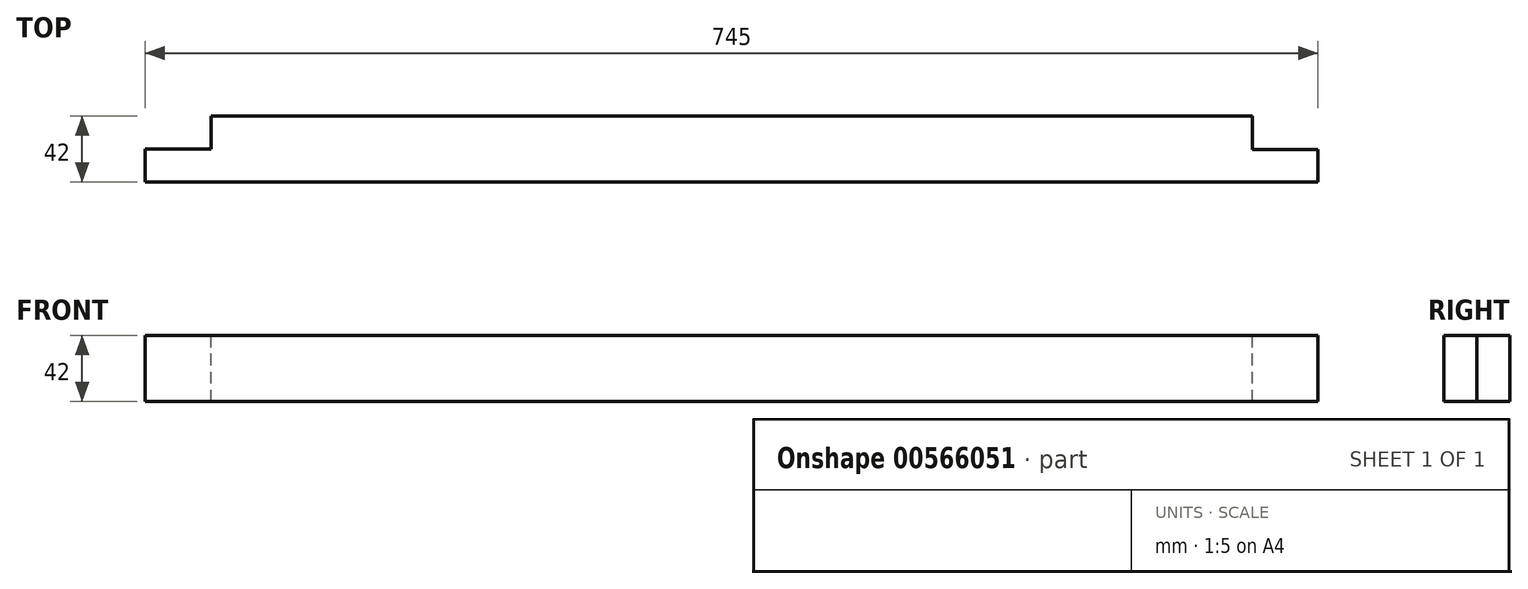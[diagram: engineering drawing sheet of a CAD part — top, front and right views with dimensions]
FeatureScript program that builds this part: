
annotation { "Feature Type Name" : "Feature", "Feature Type Description" : "" }
export const myFeature = defineFeature(function(context is Context, id is Id, definition is map)
    precondition{}
    {
        {
            var Q0;
            Q0=qCreatedBy(makeId("Top.planeOp"),FACE);
            var sketch = newSketch(context, id + "F0", { "sketchPlane" : qUnion([Q0])});
            skLineSegment(sketch, "E0.bottom", {"start": v(-348.32, -28.54) * mm, "end": v(396.68, -28.54) * mm});
            skLineSegment(sketch, "E0.top", {"start": v(-348.32, -70.54) * mm, "end": v(396.68, -70.54) * mm});
            skLineSegment(sketch, "E0.left", {"start": v(-348.32, -28.54) * mm, "end": v(-348.32, -70.54) * mm});
            skLineSegment(sketch, "E0.right", {"start": v(396.68, -28.54) * mm, "end": v(396.68, -70.54) * mm});
            skSolve(sketch);
        }
        {
            var Q0;
            Q0 = qSketchRegion(id + "F0", true);
            extrude(context, id + "F1", {"entities" : qUnion([Q0]), "depth" : 42 * mm, "offsetDistance" : 25 * mm});
        }
        {
            var Q0;
            Q0=makeQuery(id+"F1.opExtrude","CAP_FACE",FACE,{"disambiguationData":[OSD([sQuery(id+"F0.wireOp",EDGE,"E0.bottom"),sQuery(id+"F0.wireOp",EDGE,"E0.top"),sQuery(id+"F0.wireOp",EDGE,"E0.left"),sQuery(id+"F0.wireOp",EDGE,"E0.right")])],"isStart":false});
            var sketch = newSketch(context, id + "F2", { "sketchPlane" : qUnion([Q0])});
            skLineSegment(sketch, "E1.bottom", {"start": v(396.68, -28.54) * mm, "end": v(354.96, -28.54) * mm});
            skLineSegment(sketch, "E1.top", {"start": v(396.68, -49.82) * mm, "end": v(354.96, -49.82) * mm});
            skLineSegment(sketch, "E1.left", {"start": v(396.68, -28.54) * mm, "end": v(396.68, -49.82) * mm});
            skLineSegment(sketch, "E1.right", {"start": v(354.96, -28.54) * mm, "end": v(354.96, -49.82) * mm});
            skSolve(sketch);
        }
        {
            var Q0;
            Q0 = qSketchRegion(id + "F2", true);
            extrude(context, id + "F3", {"entities" : qUnion([Q0]), "operationType" : NewBodyOperationType.REMOVE, "oppositeDirection" : true, "depth" : 42 * mm, "offsetDistance" : 25 * mm});
        }
        {
            var Q0;
            Q0=makeQuery(id+"F1.opExtrude","CAP_FACE",FACE,{"disambiguationData":[OSD([sQuery(id+"F0.wireOp",EDGE,"E0.bottom"),sQuery(id+"F0.wireOp",EDGE,"E0.top"),sQuery(id+"F0.wireOp",EDGE,"E0.left"),sQuery(id+"F0.wireOp",EDGE,"E0.right")])],"isStart":false});
            var sketch = newSketch(context, id + "F4", { "sketchPlane" : qUnion([Q0])});
            skLineSegment(sketch, "E2.bottom", {"start": v(-348.32, -28.54) * mm, "end": v(-306.32, -28.54) * mm});
            skLineSegment(sketch, "E2.top", {"start": v(-348.32, -49.54) * mm, "end": v(-306.32, -49.54) * mm});
            skLineSegment(sketch, "E2.left", {"start": v(-348.32, -28.54) * mm, "end": v(-348.32, -49.54) * mm});
            skLineSegment(sketch, "E2.right", {"start": v(-306.32, -28.54) * mm, "end": v(-306.32, -49.54) * mm});
            skSolve(sketch);
        }
        {
            var Q0;
            Q0 = qSketchRegion(id + "F4", true);
            extrude(context, id + "F5", {"entities" : qUnion([Q0]), "operationType" : NewBodyOperationType.REMOVE, "oppositeDirection" : true, "depth" : 42 * mm, "offsetDistance" : 25 * mm});
        }
    });
